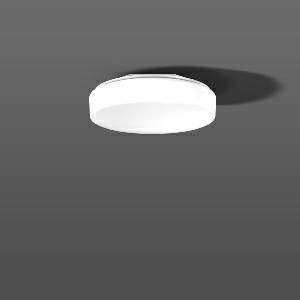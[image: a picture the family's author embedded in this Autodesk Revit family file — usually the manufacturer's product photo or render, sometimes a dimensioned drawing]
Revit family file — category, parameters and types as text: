
# Revit family: flat_polymero_kreis_672092_002_6_1_04_2599
name_source: partatom
category: Lighting Fixtures
units: mm (PartAtom-declared; Revit-internal decimal feet)

## family parameters
Cut with Voids When Loaded = No
Host = Face
Light Source = No
Part Type = Normal
Room Calculation Point = No
Round Connector Dimension = Use Diameter
Shared = No

## types (1)
- FLAT POLYMERO KREIS (1 x LED Modul 840, 1800 lm, 4000)
    Apparent Load = 15 VA
    CIE Flux Codes = 43 73 91 87 100
    Color Rendering = 80
    Color Temperature = 4000
    Default Elevation = 1800 mm  [stored 5.90551 ft]
    Description = Series: FLAT POLYMERO KREIS
Decorative round surface-mounted luminaire. For escape route illumination. Base: metal, powder-coated. Diffuser made of plastic (polycarbonate), opal, shockproof. Diffuser fastening: patented push system. Suitable for Ceiling mounting, Wall (surface). Self-contained system with automatic self-test and feedback to the RZB monitoring system MULTIDIGIT. 
Colour: white
Diameter: 360 mm
Height: 109 mm
Weight: 1.88 kg
Operating mode: Combined NL readiness
Duration time: 3 h
Lamp: LED
Socket: without socket
Colour temperature: 4000K
Colour rendering index (CRI): 80
System power: 15 W
Rated luminous flux: 1800 lm
Luminous flux, emergency: 210 lm
System power, emergency: -
Control gear: Regulated power supply
Protection class: I
Type of protection: IP 40
    Height = 109 mm
    Lamp = 1 x LED Modul 840
    Lamp Light Flux = 1800 lm
    Lamp count = 1
    Length = 360 mm
    Lifetime = 50000 h
    Luminous efficacy = 120 lm/W
    Manufacturer = RZB
    ModVariant = No
    Model = 672092.002.6.1.04
    Mounting Place = Ceiling
    Mounting Type = Surface mounted
    Number of Poles = 1
    OnlyDefault = Yes
    Power Factor = 1
    Product Name = FLAT POLYMERO KREIS
    Product group = Surface mounted ceiling and wall luminaires
    ProductGroupID = 305
    Protection Class = Protection class I
    Protection Degree = Degree of protection
    RLX_Detail_Level = 1
    RLX_Emergency_Light_Flux = 210 lm
    RLX_Emergency_Type = 3
    RLX_Emergency_Type_DB = Yes
    RlxData = <blob elided: 52137 chars, md5=ff5cefc2>
    Socket = socket
    Standby Power = 0 W
    System Light Flux = 1800 lm
    System Power = 15 W
    Type Comments = Product without accessories
    Type Image = 672092.002.1.jpg
    URL = http://relux.com
    VarID = ---
    Voltage = 0 V
    Weight = 0.00 kg
    Width = 0 mm  [stored 0 ft]

note: [stored X ft] marks values corroborated as IEEE doubles in the binary element streams (Revit-internal decimal feet)

## geometry (parser evidence)
native form markers: Blend x4, Sweep x14
no freeform markers — native parametric forms only
